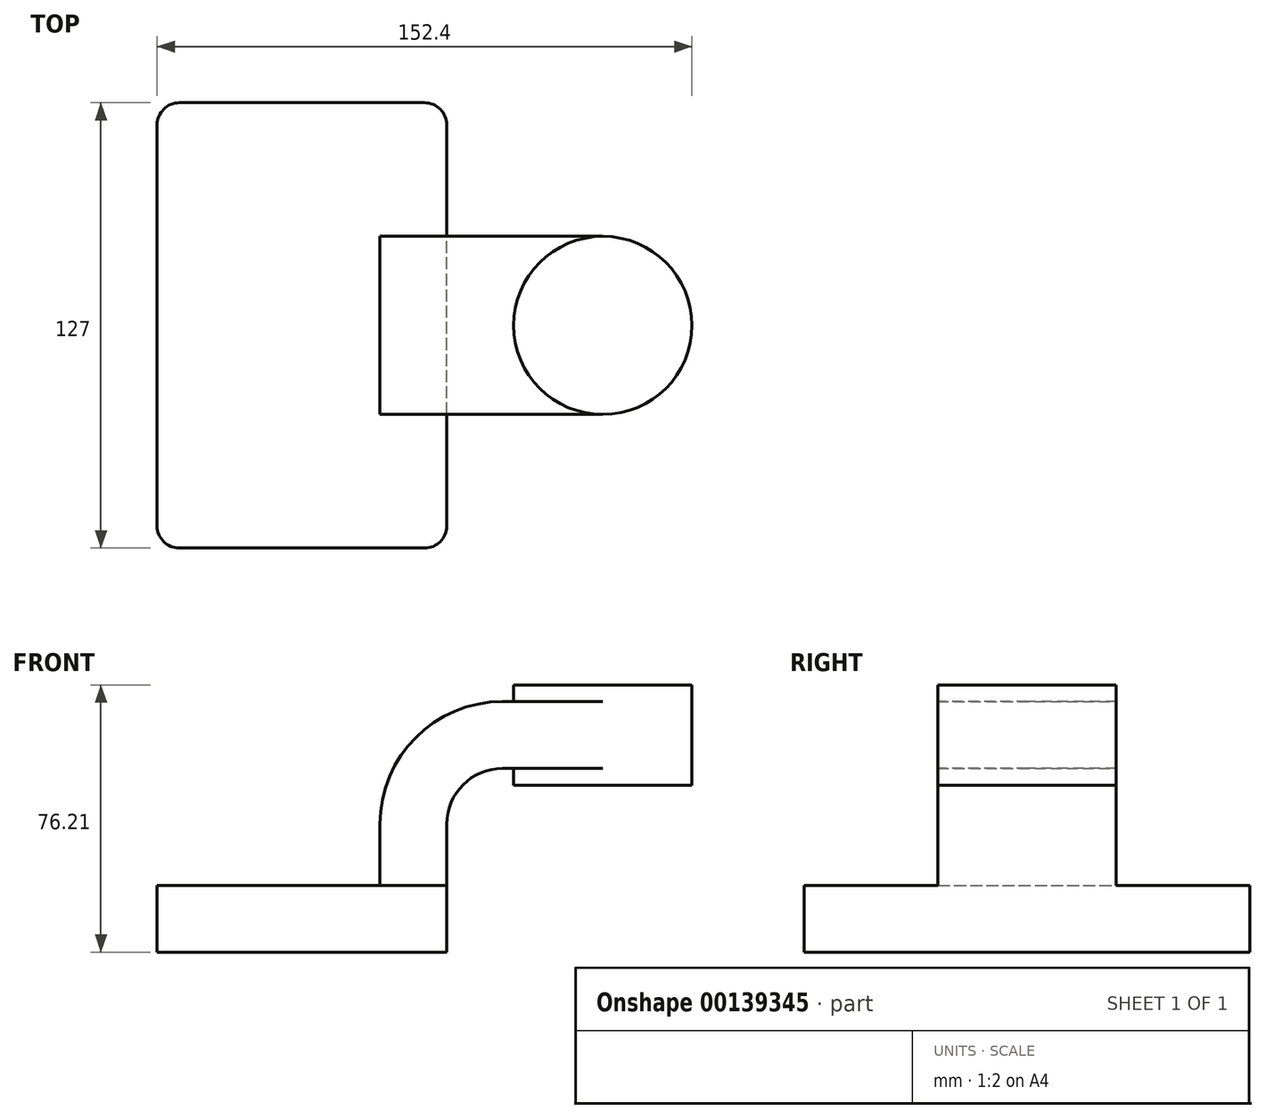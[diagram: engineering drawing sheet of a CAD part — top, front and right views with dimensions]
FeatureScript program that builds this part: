
annotation { "Feature Type Name" : "Feature", "Feature Type Description" : "" }
export const myFeature = defineFeature(function(context is Context, id is Id, definition is map)
    precondition{}
    {
        {
            var Q0;
            Q0=qCreatedBy(makeId("Front.planeOp"),FACE);
            var sketch = newSketch(context, id + "F0", { "sketchPlane" : qUnion([Q0])});
            skLineSegment(sketch, "E0.bottom", {"start": v(-41.27, -9.53) * mm, "end": v(41.28, -9.53) * mm});
            skLineSegment(sketch, "E0.top", {"start": v(-41.28, 9.53) * mm, "end": v(41.28, 9.53) * mm});
            skLineSegment(sketch, "E0.left", {"start": v(-41.28, -9.53) * mm, "end": v(-41.28, 9.53) * mm});
            skLineSegment(sketch, "E0.right", {"start": v(41.28, -9.53) * mm, "end": v(41.28, 9.52) * mm});
            skPoint(sketch, "E0.middle", {"position": v(0, 0) * mm});
            skLineSegment(sketch, "E1.bottom", {"start": v(111.13, 38.1) * mm, "end": v(60.33, 38.1) * mm});
            skLineSegment(sketch, "E1.top", {"start": v(111.13, 66.67) * mm, "end": v(60.33, 66.67) * mm});
            skLineSegment(sketch, "E1.left", {"start": v(111.13, 38.1) * mm, "end": v(111.13, 66.67) * mm});
            skLineSegment(sketch, "E1.right", {"start": v(60.33, 38.1) * mm, "end": v(60.33, 66.67) * mm});
            skPoint(sketch, "E1.middle", {"position": v(85.73, 52.39) * mm});
            skLineSegment(sketch, "E2", {"start": v(41.28, 9.52) * mm, "end": v(41.28, 26.99) * mm});
            skArc(sketch, "E3", {"start": v(41.27, 26.99) * mm, "mid": v(45.92, 38.21) * mm, "end": v(57.15, 42.86) * mm});
            skArc(sketch, "E4.1", {"start": v(22.22, 26.99) * mm, "mid": v(32.45, 51.68) * mm, "end": v(57.15, 61.91) * mm});
            skLineSegment(sketch, "E4.2", {"start": v(22.22, 9.52) * mm, "end": v(22.22, 26.99) * mm});
            skLineSegment(sketch, "E5", {"start": v(57.15, 42.86) * mm, "end": v(85.73, 42.86) * mm});
            skLineSegment(sketch, "E6", {"start": v(57.15, 61.91) * mm, "end": v(85.73, 61.91) * mm});
            skLineSegment(sketch, "E7", {"start": v(85.73, 38.1) * mm, "end": v(85.73, 66.67) * mm});
            skFitSpline(sketch, "E8", {"points": [v(-41.27, 9.53) * mm, v(57.15, 61.91) * mm], "startDerivative": vector(-0.15, 101.62) * mm, "endDerivative": vector(126.68, -0.7) * mm});
            skSolve(sketch);
        }
        {
            var Q0;
            Q0=makeQuery(id+"F0.imprint","IMPRINT",FACE,{"disambiguationData":[TD([[makeQuery(id+"F0.imprint","IMPRINT",EDGE,{"derivedFrom":sQuery(id+"F0.wireOp",EDGE,"E0.bottom")}),1.0]])]});
            extrude(context, id + "F1", {"entities" : qUnion([Q0]), "endBound" : BoundingType.SYMMETRIC, "depth" : 127 * mm});
        }
        {
            var Q0;
            {var subQ1=sQuery(id+"F0.wireOp",EDGE,"E2");Q0=makeQuery(id+"F0.imprint","IMPRINT",FACE,{"disambiguationData":[TD([[makeQuery(id+"F0.imprint","IMPRINT",EDGE,{"derivedFrom":subQ1}),1.0]])]});}
            var Q1;
            {var subQ0=sQuery(id+"F0.wireOp",EDGE,"E5");var subQ1=sQuery(id+"F0.wireOp",EDGE,"E1.right");var subQ2=makeQuery(id+"F0.imprint","INTERSECT",VERTEX,{"derivedFrom":[subQ1,subQ0]});Q1=makeQuery(id+"F0.imprint","IMPRINT",FACE,{"disambiguationData":[TD([[makeQuery(id+"F0.imprint","IMPRINT",EDGE,{"disambiguationData":[TD([[subQ2,-1.0]])],"derivedFrom":subQ1}),-1.0]])]});}
            extrude(context, id + "F2", {"entities" : qUnion([Q0, Q1]), "operationType" : NewBodyOperationType.ADD, "endBound" : BoundingType.SYMMETRIC, "depth" : 50.8 * mm});
        }
        {
            var Q0;
            Q0=makeQuery(id+"F0.imprint","IMPRINT",FACE,{"disambiguationData":[TD([[makeQuery(id+"F0.imprint","IMPRINT",EDGE,{"derivedFrom":sQuery(id+"F0.wireOp",EDGE,"E4.1")}),1.0]])]});
            extrude(context, id + "F3", {"entities" : qUnion([Q0]), "operationType" : NewBodyOperationType.ADD, "endBound" : BoundingType.SYMMETRIC, "depth" : 15.88 * mm});
        }
        {
            var Q0;
            {var subQ0=sQuery(id+"F0.wireOp",EDGE,"E1.left");Q0=makeQuery(id+"F0.imprint","IMPRINT",FACE,{"disambiguationData":[TD([[makeQuery(id+"F0.imprint","IMPRINT",EDGE,{"derivedFrom":subQ0}),1.0]])]});}
            var Q1;
            Q1=sQuery(id+"F0.wireOp",EDGE,"E7");
            revolve(context, id + "F4", {"operationType" : NewBodyOperationType.ADD, "entities" : qUnion([Q0]), "axis" : qUnion([Q1]), "revolveType" : RevolveType.FULL});
        }
        {
            var Q0;
            Q0=makeQuery(id+"F1.opExtrude","CAP_EDGE",EDGE,{"disambiguationData":[OSD([sQuery(id+"F0.wireOp",EDGE,"E0.left")])],"isStart":true});
            var Q1;
            Q1=makeQuery(id+"F1.opExtrude","CAP_EDGE",EDGE,{"disambiguationData":[OSD([sQuery(id+"F0.wireOp",EDGE,"E0.left")])],"isStart":false});
            var Q2;
            Q2=makeQuery(id+"F1.opExtrude","CAP_EDGE",EDGE,{"disambiguationData":[OSD([sQuery(id+"F0.wireOp",EDGE,"E0.right")])],"isStart":false});
            var Q3;
            Q3=makeQuery(id+"F1.opExtrude","CAP_EDGE",EDGE,{"disambiguationData":[OSD([sQuery(id+"F0.wireOp",EDGE,"E0.right")])],"isStart":true});
            fillet(context, id + "F5", {"entities" : qUnion([Q0, Q1, Q2, Q3]), "radius" : 6.35 * mm, "tangentPropagation" : true, "allowEdgeOverflow" : false});
        }
    });
